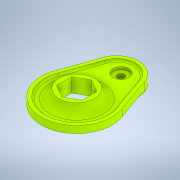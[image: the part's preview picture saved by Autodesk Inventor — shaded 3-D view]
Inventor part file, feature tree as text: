
AUTODESK INVENTOR PART (.ipt)
format: ipt  version: 2021 (Build 250183000, 183)  size: 218,112 bytes
history: native  units: mm
features: extrude x7, sketch x6, fillet x4
ambient origin geometry x8: Origin, YZ Plane, XZ Plane, XY Plane, X Axis, Y Axis, Z Axis, Center Point
bodies: Solid1 (feature_tree)
feature tree (17):
  extrude  "Extrusion1"  Depth=8.0mm TaperAngle=0.0deg
  extrude  "Extrusion2"  Depth=10.0mm
  fillet  "Fillet1"  Radius=10.0mm
  fillet  "Fillet2"  Radius=1000.0mm
  extrude  "Extrusion3"  Depth=4.0mm
  fillet  "Fillet3"  Radius=2.0mm
  extrude  "Extrusion4"  Depth=2.0mm TaperAngle=0.0deg
  extrude  "Extrusion5"  Depth=10.0mm TaperAngle=0.0deg
  fillet  "Fillet4"  Radius=10.0mm
  sketch  "Sketch6"  dims[d21=18.0mm d22=8.0mm d23=5.0mm d24=3.0mm d25=0.0mm d26=0.0mm d27=0.0mm]
  extrude  "Extrusion6"  Depth=8.0mm
  extrude  "Extrusion7"  Depth=5.0mm
  sketch  "Sketch1"  dims[d0=80.0mm d1=8.0mm d2=0.0mm]
  sketch  "Sketch2"  dims[d3=50.0mm d4=45.0mm d5=10.0mm d6=0.0mm d7=1000.0mm]
  sketch  "Sketch3"  dims[d8=2.0mm d9=4.0mm d10=2.0mm d11=0.0mm]
  sketch  "Sketch4"  dims[d12=2.0mm d15=2.0mm d16=0.0mm]
  sketch  "Sketch5"  dims[d17=40.0mm d18=10.0mm d19=0.0mm d20=10.0mm]
